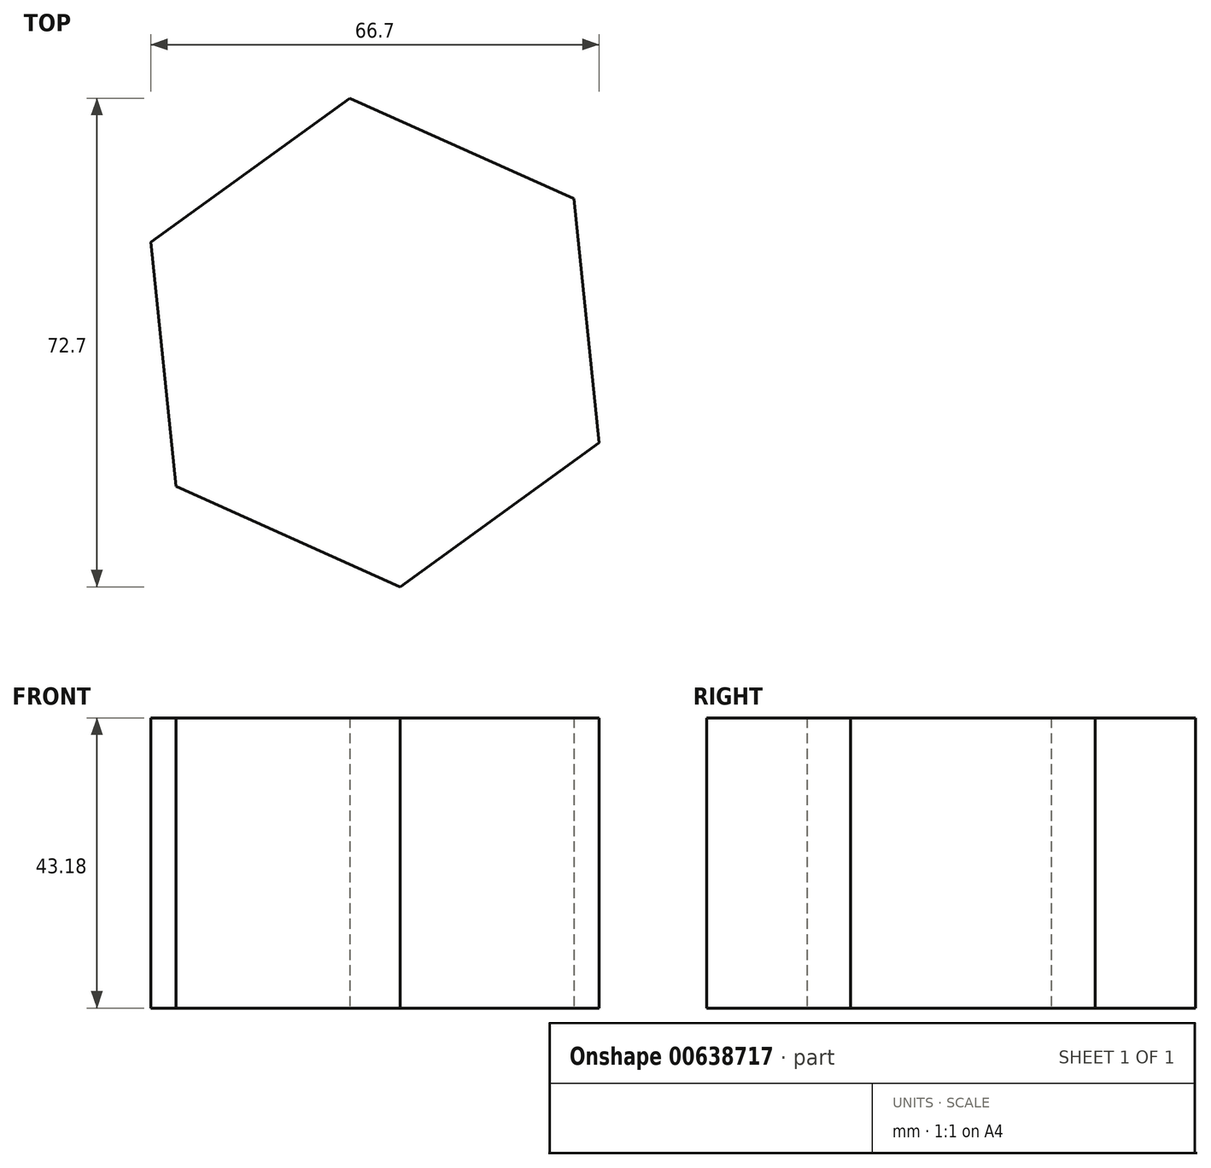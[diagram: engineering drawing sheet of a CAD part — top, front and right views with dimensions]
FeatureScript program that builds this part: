
annotation { "Feature Type Name" : "Feature", "Feature Type Description" : "" }
export const myFeature = defineFeature(function(context is Context, id is Id, definition is map)
    precondition{}
    {
        {
            var Q0;
            Q0=qCreatedBy(makeId("Top.planeOp"),FACE);
            var sketch = newSketch(context, id + "F0", { "sketchPlane" : qUnion([Q0])});
            skCircle(sketch, "E0.cCircle", {"center": v(0, 0) * mm, "radius": 31.65 * mm, "construction": true});
            skLineSegment(sketch, "E0.0", {"start": v(-33.35, 14.93) * mm, "end": v(-3.75, 36.35) * mm});
            skLineSegment(sketch, "E0.1", {"start": v(-3.75, 36.35) * mm, "end": v(29.6, 21.42) * mm});
            skLineSegment(sketch, "E0.2", {"start": v(29.6, 21.42) * mm, "end": v(33.35, -14.93) * mm});
            skLineSegment(sketch, "E0.3", {"start": v(33.35, -14.93) * mm, "end": v(3.75, -36.35) * mm});
            skLineSegment(sketch, "E0.4", {"start": v(3.75, -36.35) * mm, "end": v(-29.6, -21.42) * mm});
            skLineSegment(sketch, "E0.5", {"start": v(-29.6, -21.42) * mm, "end": v(-33.35, 14.93) * mm});
            skPoint(sketch, "E0.0.midPoint", {"position": v(-18.55, 25.64) * mm});
            skSolve(sketch);
        }
        {
            var Q0;
            Q0=makeQuery(id+"F0.imprint","IMPRINT",FACE,{"disambiguationData":[TD([[makeQuery(id+"F0.imprint","IMPRINT",EDGE,{"derivedFrom":sQuery(id+"F0.wireOp",EDGE,"E0.0")}),-1.0]])]});
            extrude(context, id + "F1", {"entities" : qUnion([Q0]), "depth" : 43.18 * mm, "offsetDistance" : 25.4 * mm});
        }
    });
